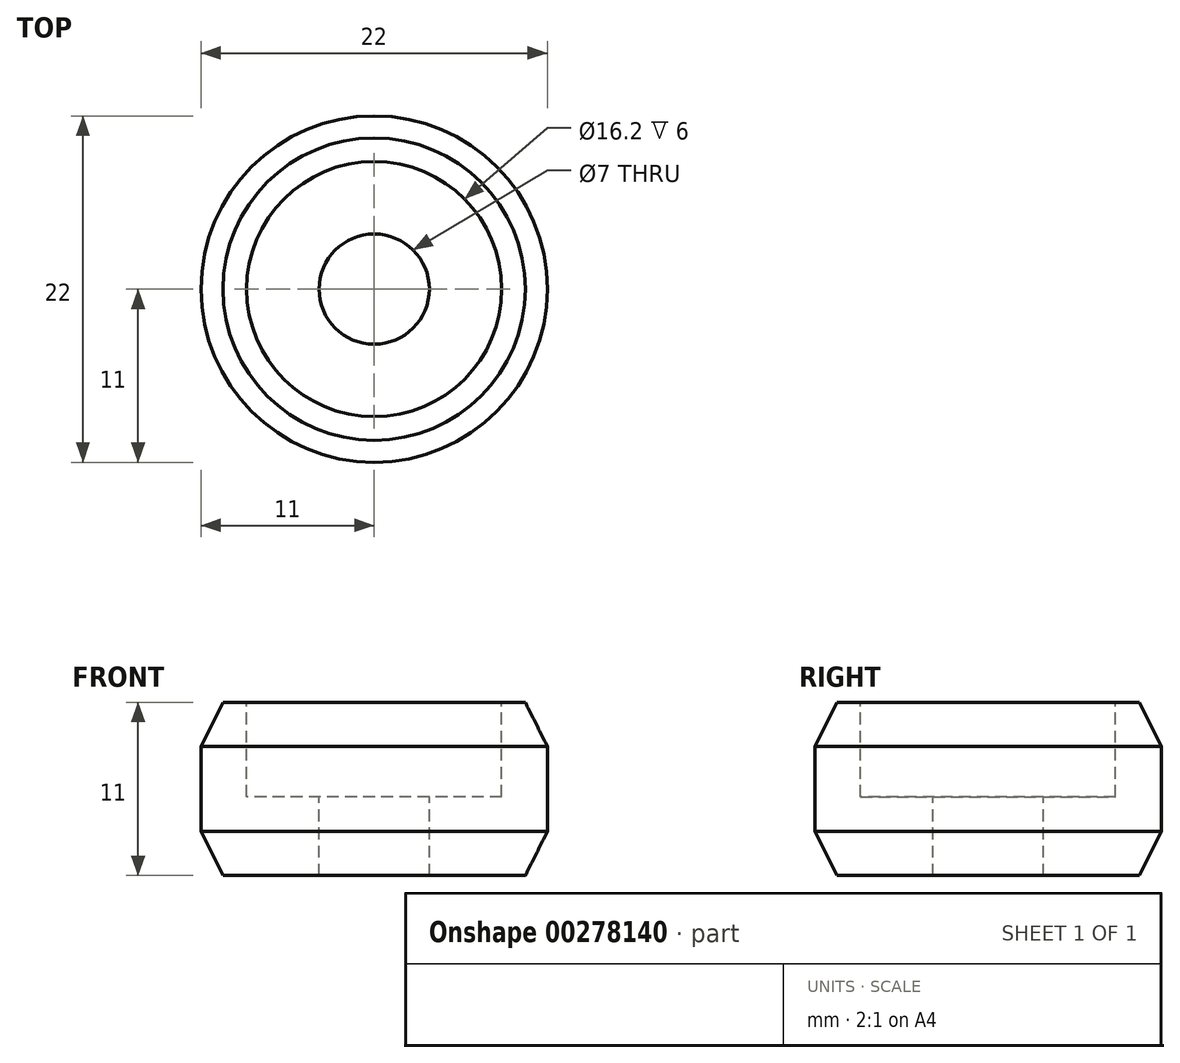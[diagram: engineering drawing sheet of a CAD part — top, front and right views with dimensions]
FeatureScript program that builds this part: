
annotation { "Feature Type Name" : "Feature", "Feature Type Description" : "" }
export const myFeature = defineFeature(function(context is Context, id is Id, definition is map)
    precondition{}
    {
        {
            var Q0;
            Q0=qCreatedBy(makeId("Top.planeOp"),FACE);
            var sketch = newSketch(context, id + "F0", { "sketchPlane" : qUnion([Q0])});
            skCircle(sketch, "E0", {"center": v(0, 0) * mm, "radius": 11 * mm});
            skSolve(sketch);
        }
        {
            var Q0;
            Q0=makeQuery(id+"F0.imprint","IMPRINT",FACE,{"disambiguationData":[TD([[makeQuery(id+"F0.imprint","IMPRINT",EDGE,{"derivedFrom":sQuery(id+"F0.wireOp",EDGE,"E0")}),1.0]])]});
            extrude(context, id + "F1", {"entities" : qUnion([Q0]), "depth" : 5.5 * mm, "hasSecondDirection" : true, "secondDirectionOppositeDirection" : true, "secondDirectionDepth" : 5.5 * mm});
        }
        {
            var Q0;
            Q0=makeQuery(id+"F1.opExtrude","CAP_FACE",FACE,{"disambiguationData":[OSD([sQuery(id+"F0.wireOp",EDGE,"E0")])],"isStart":false});
            var sketch = newSketch(context, id + "F2", { "sketchPlane" : qUnion([Q0])});
            skCircle(sketch, "E1", {"center": v(0, 0) * mm, "radius": 9.6 * mm});
            skSolve(sketch);
        }
        {
            var Q0;
            Q0=makeQuery(id+"F1.opExtrude","CAP_EDGE",EDGE,{"disambiguationData":[OSD([sQuery(id+"F0.wireOp",EDGE,"E0")])],"isStart":false});
            chamfer(context, id + "F3", {"entities" : qUnion([Q0]), "chamferType" : ChamferType.TWO_OFFSETS, "width1" : 1.4 * mm, "oppositeDirection" : false, "width2" : 2.8 * mm, "tangentPropagation" : true});
        }
        {
            var Q0;
            Q0=makeQuery(id+"F1.opExtrude","CAP_EDGE",EDGE,{"disambiguationData":[OSD([sQuery(id+"F0.wireOp",EDGE,"E0")])],"isStart":true});
            chamfer(context, id + "F4", {"entities" : qUnion([Q0]), "chamferType" : ChamferType.TWO_OFFSETS, "width1" : 2.8 * mm, "oppositeDirection" : false, "width2" : 1.4 * mm, "tangentPropagation" : true});
        }
        {
            var Q0;
            Q0=makeQuery(id+"F1.opExtrude","CAP_FACE",FACE,{"disambiguationData":[OSD([sQuery(id+"F0.wireOp",EDGE,"E0")])],"isStart":false});
            var sketch = newSketch(context, id + "F5", { "sketchPlane" : qUnion([Q0])});
            skCircle(sketch, "E2", {"center": v(0, 0) * mm, "radius": 8.1 * mm});
            skSolve(sketch);
        }
        {
            var Q0;
            Q0=makeQuery(id+"F5.imprint","IMPRINT",FACE,{"disambiguationData":[TD([[makeQuery(id+"F5.imprint","IMPRINT",EDGE,{"derivedFrom":sQuery(id+"F5.wireOp",EDGE,"E2")}),1.0]])]});
            extrude(context, id + "F6", {"entities" : qUnion([Q0]), "operationType" : NewBodyOperationType.REMOVE, "oppositeDirection" : true, "depth" : 6 * mm});
        }
        {
            var Q0;
            Q0=makeQuery(id+"F6.boolean.opBoolean","COPY",FACE,{"derivedFrom":makeQuery(id+"F6.opExtrude","CAP_FACE",FACE,{"disambiguationData":[OSD([sQuery(id+"F5.wireOp",EDGE,"E2")])],"isStart":false})});
            var sketch = newSketch(context, id + "F7", { "sketchPlane" : qUnion([Q0])});
            skCircle(sketch, "E3", {"center": v(0, 0) * mm, "radius": 3.5 * mm});
            skSolve(sketch);
        }
        {
            var Q0;
            Q0=makeQuery(id+"F7.imprint","IMPRINT",FACE,{"disambiguationData":[TD([[makeQuery(id+"F7.imprint","IMPRINT",EDGE,{"derivedFrom":sQuery(id+"F7.wireOp",EDGE,"E3")}),1.0]])]});
            extrude(context, id + "F8", {"entities" : qUnion([Q0]), "operationType" : NewBodyOperationType.REMOVE, "endBound" : BoundingType.UP_TO_NEXT, "oppositeDirection" : true, "depth" : 25 * mm});
        }
    });
